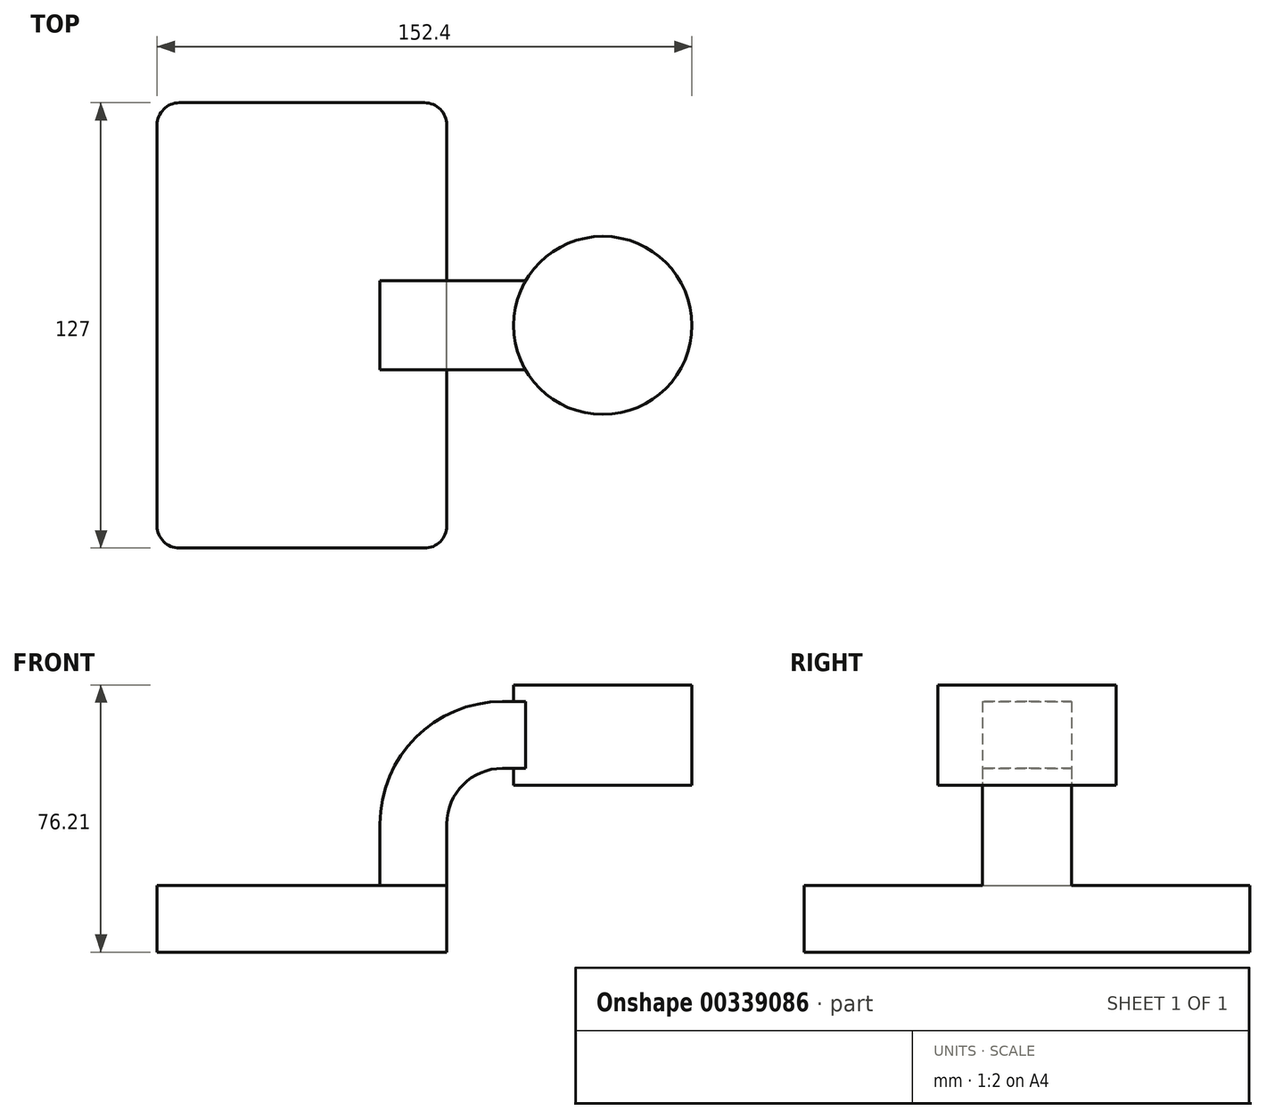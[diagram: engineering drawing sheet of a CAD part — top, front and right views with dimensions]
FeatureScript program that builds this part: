
annotation { "Feature Type Name" : "Feature", "Feature Type Description" : "" }
export const myFeature = defineFeature(function(context is Context, id is Id, definition is map)
    precondition{}
    {
        {
            var Q0;
            Q0=qCreatedBy(makeId("Front.planeOp"),FACE);
            var sketch = newSketch(context, id + "F0", { "sketchPlane" : qUnion([Q0])});
            skLineSegment(sketch, "E0.bottom", {"start": v(41.28, -9.53) * mm, "end": v(-41.28, -9.53) * mm});
            skLineSegment(sketch, "E0.top", {"start": v(41.28, 9.52) * mm, "end": v(-41.28, 9.52) * mm});
            skLineSegment(sketch, "E0.left", {"start": v(41.28, -9.52) * mm, "end": v(41.28, 9.53) * mm});
            skLineSegment(sketch, "E0.right", {"start": v(-41.28, -9.52) * mm, "end": v(-41.28, 9.53) * mm});
            skPoint(sketch, "E0.middle", {"position": v(0, 0) * mm});
            skLineSegment(sketch, "E1.bottom", {"start": v(85.72, 38.1) * mm, "end": v(60.33, 38.1) * mm});
            skLineSegment(sketch, "E1.top", {"start": v(111.12, 66.67) * mm, "end": v(60.33, 66.67) * mm});
            skLineSegment(sketch, "E1.left", {"start": v(111.12, 38.1) * mm, "end": v(111.12, 66.68) * mm});
            skLineSegment(sketch, "E1.right", {"start": v(60.32, 38.1) * mm, "end": v(60.32, 66.68) * mm});
            skPoint(sketch, "E1.middle", {"position": v(85.72, 52.39) * mm});
            skLineSegment(sketch, "E2", {"start": v(41.28, 9.53) * mm, "end": v(41.28, 27) * mm});
            skArc(sketch, "E3", {"start": v(41.27, 27) * mm, "mid": v(45.92, 38.23) * mm, "end": v(57.15, 42.88) * mm});
            skLineSegment(sketch, "E4", {"start": v(57.15, 42.88) * mm, "end": v(85.72, 42.88) * mm});
            skPoint(sketch, "E4.endSnap0", {"position": v(85.72, 38.1) * mm});
            skLineSegment(sketch, "E5", {"start": v(85.72, 38.1) * mm, "end": v(111.12, 38.1) * mm});
            skLineSegment(sketch, "E6.0", {"start": v(57.15, 61.93) * mm, "end": v(85.73, 61.93) * mm});
            skArc(sketch, "E6.1", {"start": v(22.23, 27) * mm, "mid": v(32.45, 51.7) * mm, "end": v(57.15, 61.93) * mm});
            skLineSegment(sketch, "E6.2", {"start": v(22.23, 9.52) * mm, "end": v(22.23, 27) * mm});
            skLineSegment(sketch, "E7", {"start": v(85.72, 38.1) * mm, "end": v(85.72, 66.68) * mm});
            skFitSpline(sketch, "E8", {"points": [v(-41.28, 9.52) * mm, v(57.15, 61.93) * mm], "startDerivative": vector(0, 80.45) * mm, "endDerivative": vector(151.05, 0) * mm});
            skSolve(sketch);
        }
        {
            var Q0;
            Q0=makeQuery(id+"F0.imprint","IMPRINT",FACE,{"disambiguationData":[TD([[makeQuery(id+"F0.imprint","IMPRINT",EDGE,{"derivedFrom":sQuery(id+"F0.wireOp",EDGE,"E0.bottom")}),-1.0]])]});
            extrude(context, id + "F1", {"entities" : qUnion([Q0]), "depth" : 127 * mm, "symmetric" : true});
        }
        {
            var Q0;
            {var subQ1=sQuery(id+"F0.wireOp",EDGE,"E2");Q0=makeQuery(id+"F0.imprint","IMPRINT",FACE,{"disambiguationData":[TD([[makeQuery(id+"F0.imprint","IMPRINT",EDGE,{"derivedFrom":subQ1}),1.0]])]});}
            var Q1;
            {var subQ0=sQuery(id+"F0.wireOp",EDGE,"E4");var subQ1=sQuery(id+"F0.wireOp",EDGE,"E1.right");var subQ2=makeQuery(id+"F0.imprint","INTERSECT",VERTEX,{"derivedFrom":[subQ1,subQ0]});Q1=makeQuery(id+"F0.imprint","IMPRINT",FACE,{"disambiguationData":[TD([[makeQuery(id+"F0.imprint","IMPRINT",EDGE,{"disambiguationData":[TD([[subQ2,-1.0]])],"derivedFrom":subQ1}),-1.0]])]});}
            extrude(context, id + "F2", {"entities" : qUnion([Q0, Q1]), "operationType" : NewBodyOperationType.ADD, "depth" : 25.4 * mm, "symmetric" : true});
        }
        {
            var Q0;
            Q0=makeQuery(id+"F0.imprint","IMPRINT",FACE,{"disambiguationData":[TD([[makeQuery(id+"F0.imprint","IMPRINT",EDGE,{"derivedFrom":sQuery(id+"F0.wireOp",EDGE,"E6.1")}),1.0]])]});
            extrude(context, id + "F3", {"entities" : qUnion([Q0]), "operationType" : NewBodyOperationType.ADD, "depth" : 16.13 * mm, "symmetric" : true});
        }
        {
            var Q0;
            {var subQ0=sQuery(id+"F0.wireOp",EDGE,"E1.left");Q0=makeQuery(id+"F0.imprint","IMPRINT",FACE,{"disambiguationData":[TD([[makeQuery(id+"F0.imprint","IMPRINT",EDGE,{"derivedFrom":subQ0}),1.0]])]});}
            var Q1;
            Q1=sQuery(id+"F0.wireOp",EDGE,"E7");
            revolve(context, id + "F4", {"operationType" : NewBodyOperationType.ADD, "entities" : qUnion([Q0]), "axis" : qUnion([Q1]), "revolveType" : RevolveType.FULL});
        }
        {
            var Q0;
            Q0=makeQuery(id+"F1.opExtrude","CAP_EDGE",EDGE,{"disambiguationData":[OSD([sQuery(id+"F0.wireOp",EDGE,"E0.left")])],"isStart":false});
            var Q1;
            Q1=makeQuery(id+"F1.opExtrude","CAP_EDGE",EDGE,{"disambiguationData":[OSD([sQuery(id+"F0.wireOp",EDGE,"E0.right")])],"isStart":false});
            var Q2;
            Q2=makeQuery(id+"F1.opExtrude","CAP_EDGE",EDGE,{"disambiguationData":[OSD([sQuery(id+"F0.wireOp",EDGE,"E0.right")])],"isStart":true});
            var Q3;
            Q3=makeQuery(id+"F1.opExtrude","CAP_EDGE",EDGE,{"disambiguationData":[OSD([sQuery(id+"F0.wireOp",EDGE,"E0.left")])],"isStart":true});
            fillet(context, id + "F5", {"entities" : qUnion([Q0, Q1, Q2, Q3]), "radius" : 6.35 * mm, "tangentPropagation" : true, "allowEdgeOverflow" : false});
        }
    });
